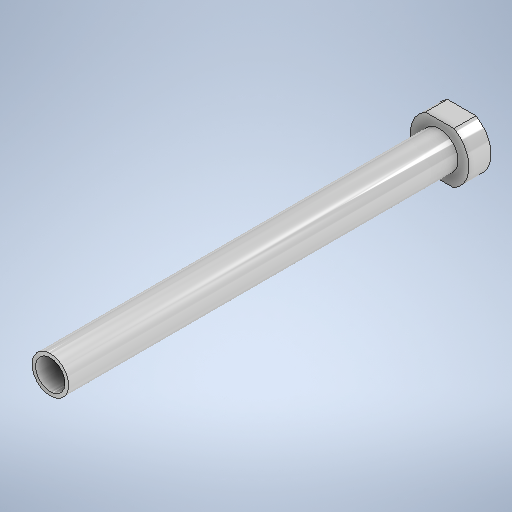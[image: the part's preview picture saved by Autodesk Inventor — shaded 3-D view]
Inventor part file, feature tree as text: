
AUTODESK INVENTOR PART (.ipt)
format: ipt  version: 2025.2 (Build 292293000, 293)  size: 284,160 bytes
history: native  units: mm
features: extrude x3, sketch x3
ambient origin geometry x8: Origin, YZ Plane, XZ Plane, XY Plane, X Axis, Y Axis, Z Axis, Center Point
bodies: Solid1 (feature_tree)
feature tree (6):
  extrude  "Extrusion1"  Depth=2.0mm
  extrude  "Extrusion2"  Depth=3.0mm TaperAngle=0.0deg
  extrude  "Extrusion3"  Depth=53.0mm TaperAngle=0.0deg
  sketch  "Sketch1"  dims[d0=8.0mm d1=2.0mm]
  sketch  "Sketch2"  dims[d2=0.0mm d3=3.0mm d4=0.0mm]
  sketch  "Sketch3"  dims[d5=5.0mm d6=53.0mm d7=0.0mm d8=4.0mm d9=8.0mm d10=0.0mm]
